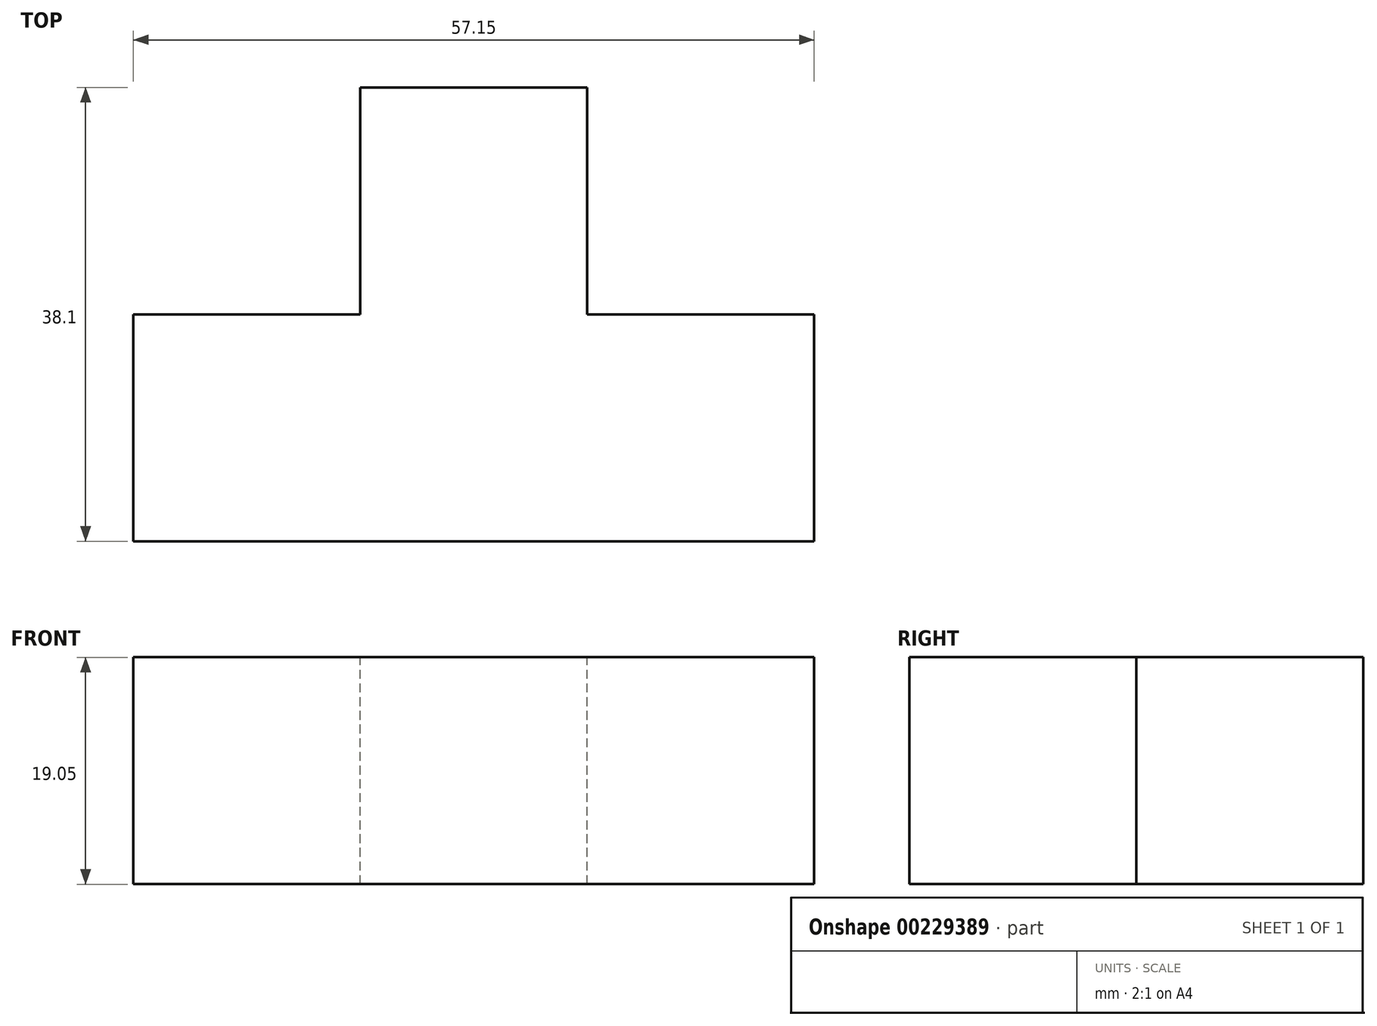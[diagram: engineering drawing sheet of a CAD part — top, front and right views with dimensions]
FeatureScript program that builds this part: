
annotation { "Feature Type Name" : "Feature", "Feature Type Description" : "" }
export const myFeature = defineFeature(function(context is Context, id is Id, definition is map)
    precondition{}
    {
        {
            var Q0;
            Q0=qCreatedBy(makeId("Front.planeOp"),FACE);
            var sketch = newSketch(context, id + "F0", { "sketchPlane" : qUnion([Q0])});
            skLineSegment(sketch, "E0.bottom", {"start": v(-29.48, 12.47) * mm, "end": v(27.67, 12.47) * mm});
            skLineSegment(sketch, "E0.top", {"start": v(-29.48, -6.58) * mm, "end": v(27.67, -6.58) * mm});
            skLineSegment(sketch, "E0.left", {"start": v(-29.48, 12.47) * mm, "end": v(-29.48, -6.58) * mm});
            skLineSegment(sketch, "E0.right", {"start": v(27.67, 12.47) * mm, "end": v(27.67, -6.58) * mm});
            skSolve(sketch);
        }
        {
            var Q0;
            Q0 = qSketchRegion(id + "F0", true);
            extrude(context, id + "F1", {"entities" : qUnion([Q0]), "oppositeDirection" : true, "depth" : 19.05 * mm});
        }
        {
            var Q0;
            Q0=makeQuery(id+"F1.opExtrude","CAP_FACE",FACE,{"disambiguationData":[OSD([sQuery(id+"F0.wireOp",EDGE,"E0.bottom"),sQuery(id+"F0.wireOp",EDGE,"E0.top"),sQuery(id+"F0.wireOp",EDGE,"E0.left"),sQuery(id+"F0.wireOp",EDGE,"E0.right")])],"isStart":false});
            var sketch = newSketch(context, id + "F2", { "sketchPlane" : qUnion([Q0])});
            skLineSegment(sketch, "E1.bottom", {"start": v(-8.62, -6.58) * mm, "end": v(10.43, -6.58) * mm});
            skLineSegment(sketch, "E1.top", {"start": v(-8.62, 12.47) * mm, "end": v(10.43, 12.47) * mm});
            skLineSegment(sketch, "E1.left", {"start": v(-8.62, -6.58) * mm, "end": v(-8.62, 12.47) * mm});
            skLineSegment(sketch, "E1.right", {"start": v(10.43, -6.58) * mm, "end": v(10.43, 12.47) * mm});
            skSolve(sketch);
        }
        {
            var Q0;
            Q0=makeQuery(id+"F2.imprint","IMPRINT",FACE,{"disambiguationData":[TD([[makeQuery(id+"F2.imprint","IMPRINT",EDGE,{"derivedFrom":sQuery(id+"F2.wireOp",EDGE,"E1.bottom")}),-1.0]])]});
            extrude(context, id + "F3", {"entities" : qUnion([Q0]), "operationType" : NewBodyOperationType.ADD, "depth" : 19.05 * mm});
        }
    });
